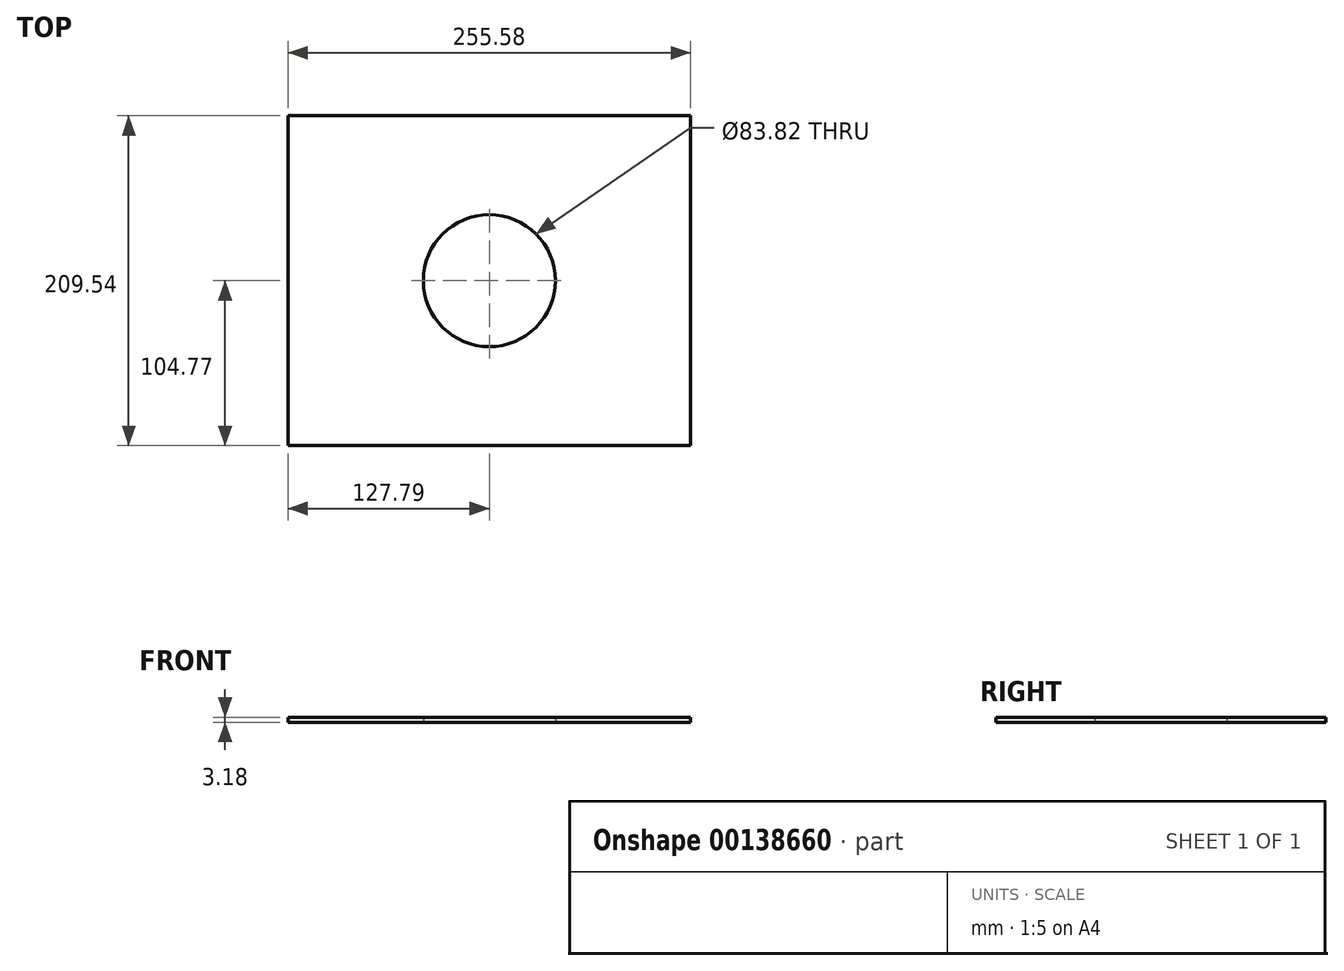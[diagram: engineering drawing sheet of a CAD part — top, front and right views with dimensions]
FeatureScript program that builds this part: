
annotation { "Feature Type Name" : "Feature", "Feature Type Description" : "" }
export const myFeature = defineFeature(function(context is Context, id is Id, definition is map)
    precondition{}
    {
        {
            var Q0;
            Q0=qCreatedBy(makeId("Top.planeOp"),FACE);
            var sketch = newSketch(context, id + "F0", { "sketchPlane" : qUnion([Q0])});
            skLineSegment(sketch, "E0.bottom", {"start": v(127.8, -104.77) * mm, "end": v(-127.8, -104.78) * mm});
            skLineSegment(sketch, "E0.top", {"start": v(127.8, 104.78) * mm, "end": v(-127.8, 104.77) * mm});
            skLineSegment(sketch, "E0.left", {"start": v(127.8, -104.77) * mm, "end": v(127.8, 104.78) * mm});
            skLineSegment(sketch, "E0.right", {"start": v(-127.8, -104.78) * mm, "end": v(-127.8, 104.77) * mm});
            skPoint(sketch, "E0.middle", {"position": v(0, 0) * mm});
            skCircle(sketch, "E1", {"center": v(0, 0) * mm, "radius": 41.91 * mm});
            skSolve(sketch);
        }
        {
            var Q0;
            Q0=makeQuery(id+"F0.imprint","IMPRINT",FACE,{"disambiguationData":[TD([[makeQuery(id+"F0.imprint","IMPRINT",EDGE,{"derivedFrom":sQuery(id+"F0.wireOp",EDGE,"E0.bottom")}),-1.0]])]});
            extrude(context, id + "F1", {"entities" : qUnion([Q0]), "depth" : 3.17 * mm});
        }
    });
